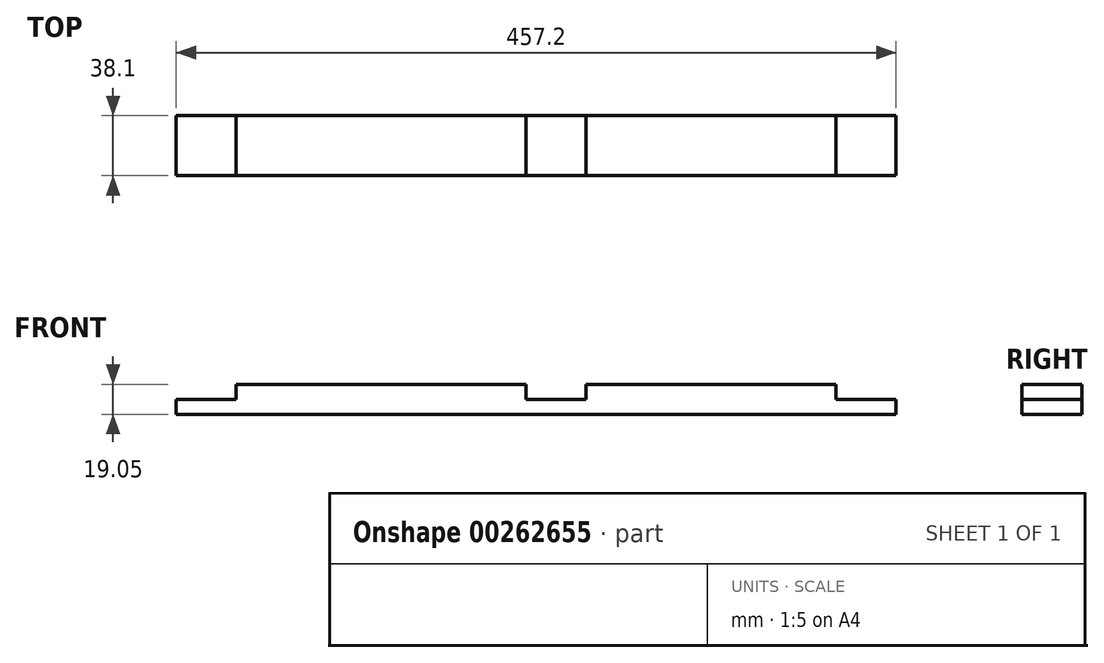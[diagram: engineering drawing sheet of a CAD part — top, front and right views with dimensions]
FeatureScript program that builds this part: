
annotation { "Feature Type Name" : "Feature", "Feature Type Description" : "" }
export const myFeature = defineFeature(function(context is Context, id is Id, definition is map)
    precondition{}
    {
        {
            var Q0;
            Q0=qCreatedBy(makeId("Front.planeOp"),FACE);
            var sketch = newSketch(context, id + "F0", { "sketchPlane" : qUnion([Q0])});
            skLineSegment(sketch, "E0", {"start": v(0, 0) * mm, "end": v(457.2, 0) * mm});
            skLineSegment(sketch, "E1", {"start": v(457.2, 0) * mm, "end": v(457.2, 9.53) * mm});
            skLineSegment(sketch, "E2", {"start": v(457.2, 9.53) * mm, "end": v(419.1, 9.53) * mm});
            skLineSegment(sketch, "E3", {"start": v(419.1, 9.53) * mm, "end": v(419.1, 19.05) * mm});
            skLineSegment(sketch, "E4", {"start": v(419.1, 19.05) * mm, "end": v(260.35, 19.05) * mm});
            skLineSegment(sketch, "E5", {"start": v(260.35, 19.05) * mm, "end": v(260.35, 9.53) * mm});
            skLineSegment(sketch, "E6", {"start": v(260.35, 9.53) * mm, "end": v(222.25, 9.52) * mm});
            skLineSegment(sketch, "E7", {"start": v(222.25, 9.52) * mm, "end": v(222.25, 19.05) * mm});
            skLineSegment(sketch, "E8", {"start": v(222.25, 19.05) * mm, "end": v(38.1, 19.05) * mm});
            skLineSegment(sketch, "E9", {"start": v(38.1, 19.05) * mm, "end": v(38.1, 9.53) * mm});
            skLineSegment(sketch, "E10", {"start": v(38.1, 9.53) * mm, "end": v(0, 9.52) * mm});
            skLineSegment(sketch, "E11", {"start": v(0, 9.52) * mm, "end": v(0, 0) * mm});
            skSolve(sketch);
        }
        {
            var Q0;
            Q0=makeQuery(id+"F0.imprint","IMPRINT",FACE,{"disambiguationData":[TD([[makeQuery(id+"F0.imprint","IMPRINT",EDGE,{"derivedFrom":sQuery(id+"F0.wireOp",EDGE,"E0")}),1.0]])]});
            extrude(context, id + "F1", {"entities" : qUnion([Q0]), "depth" : 38.1 * mm});
        }
    });
